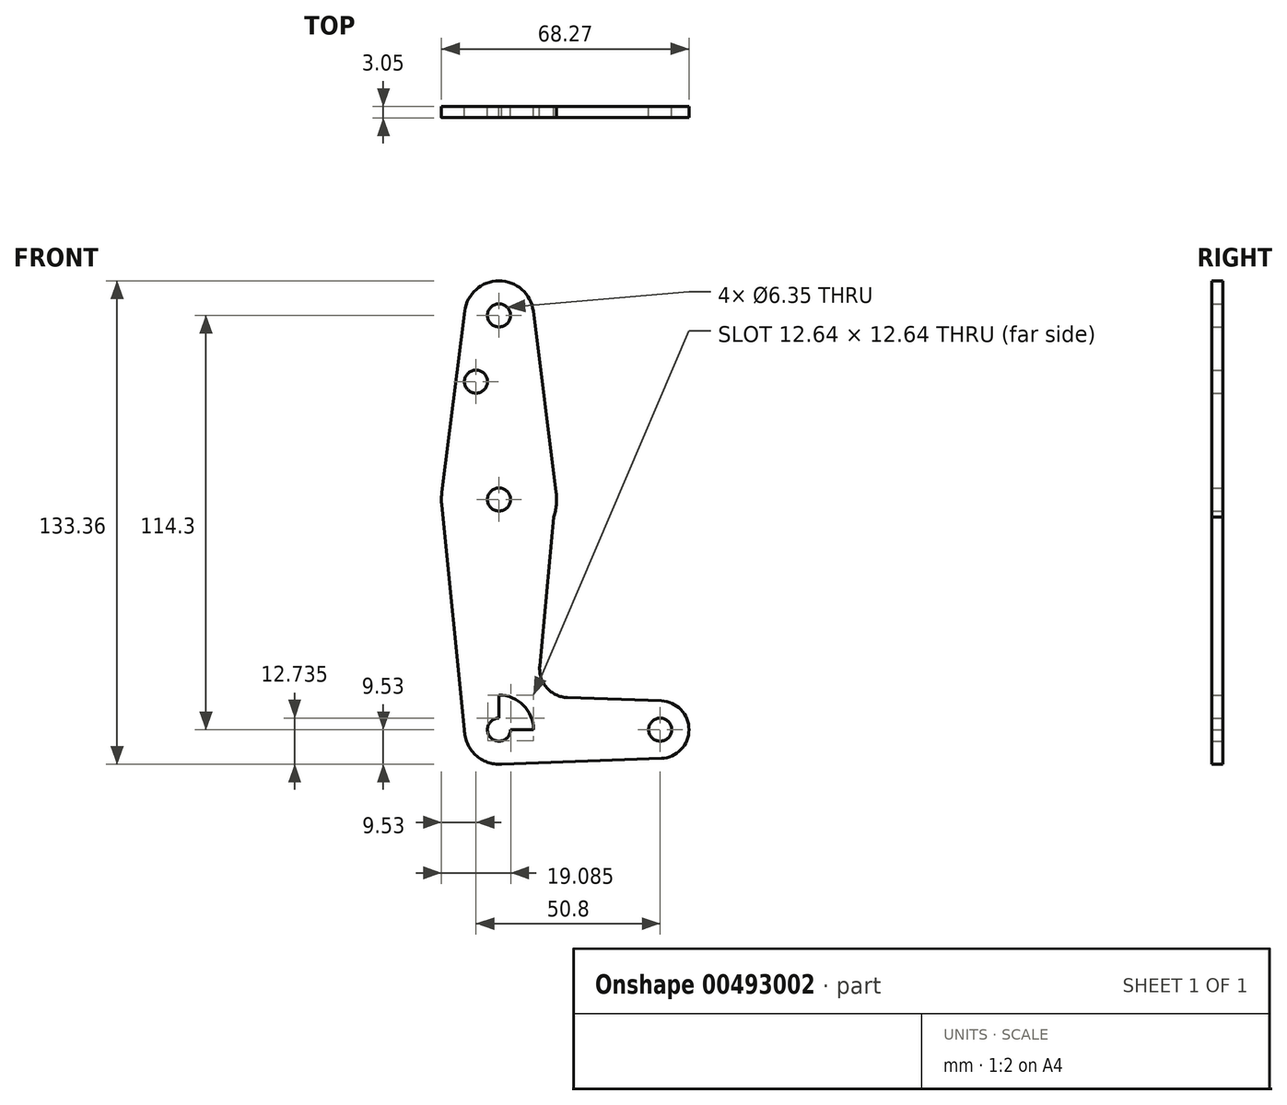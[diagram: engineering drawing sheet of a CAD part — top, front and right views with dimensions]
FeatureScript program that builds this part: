
annotation { "Feature Type Name" : "Feature", "Feature Type Description" : "" }
export const myFeature = defineFeature(function(context is Context, id is Id, definition is map)
    precondition{}
    {
        {
            var Q0;
            Q0=qCreatedBy(makeId("Front.planeOp"),FACE);
            var sketch = newSketch(context, id + "F0", { "sketchPlane" : qUnion([Q0])});
            skLineSegment(sketch, "E0", {"start": v(0, 0) * mm, "end": v(0, 114.3) * mm});
            skLineSegment(sketch, "E1", {"start": v(0, 114.3) * mm, "end": v(0, 0) * mm});
            skLineSegment(sketch, "E2", {"start": v(44.45, 0) * mm, "end": v(0, 0) * mm});
            skCircle(sketch, "E3", {"center": v(0, 114.3) * mm, "radius": 9.53 * mm});
            skCircle(sketch, "E4", {"center": v(0, 0) * mm, "radius": 9.53 * mm});
            skCircle(sketch, "E5", {"center": v(44.45, 0) * mm, "radius": 7.94 * mm});
            skCircle(sketch, "E6", {"center": v(0, 63.5) * mm, "radius": 15.88 * mm});
            skLineSegment(sketch, "E7", {"start": v(9.45, 115.5) * mm, "end": v(15.75, 65.48) * mm});
            skLineSegment(sketch, "E8", {"start": v(15.75, 65.48) * mm, "end": v(11.22, 17.55) * mm});
            skLineSegment(sketch, "E9", {"start": v(-9.45, 115.5) * mm, "end": v(-15.75, 65.48) * mm});
            skLineSegment(sketch, "E10", {"start": v(-15.75, 65.48) * mm, "end": v(-15.75, 61.52) * mm});
            skLineSegment(sketch, "E11", {"start": v(0, -9.53) * mm, "end": v(44.73, -7.93) * mm});
            skLineSegment(sketch, "E12", {"start": v(-9.53, 0) * mm, "end": v(-15.8, 61.9) * mm});
            skCircle(sketch, "E13", {"center": v(-6.35, 96.03) * mm, "radius": 3.18 * mm});
            skCircle(sketch, "E14", {"center": v(0, 63.5) * mm, "radius": 3.18 * mm});
            skCircle(sketch, "E15", {"center": v(0, 114.3) * mm, "radius": 3.18 * mm});
            skCircle(sketch, "E16", {"center": v(0, 0) * mm, "radius": 3.18 * mm});
            skCircle(sketch, "E17", {"center": v(44.45, 0) * mm, "radius": 3.18 * mm});
            skPoint(sketch, "E18.newPointA", {"position": v(0, 9.53) * mm});
            skLineSegment(sketch, "E19", {"start": v(18.86, 8.86) * mm, "end": v(44.73, 7.93) * mm});
            skArc(sketch, "E20.filletArc", {"start": v(11.22, 17.55) * mm, "mid": v(13.16, 11.56) * mm, "end": v(18.86, 8.86) * mm});
            skSolve(sketch);
        }
        {
            var Q0;
            Q0 = qSketchRegion(id + "F0", true);
            var Q1;
            {var subQ0=sQuery(id+"F0.wireOp",EDGE,"E4");var subQ1=sQuery(id+"F0.wireOp",EDGE,"E1");var subQ2=makeQuery(id+"F0.imprint","INTERSECT",VERTEX,{"derivedFrom":[subQ1,subQ0]});Q1=makeQuery(id+"F0.imprint","IMPRINT",FACE,{"disambiguationData":[TD([[makeQuery(id+"F0.imprint","IMPRINT",EDGE,{"disambiguationData":[TD([[subQ2,-1.0]])],"derivedFrom":subQ1}),1.0]])]});}
            extrude(context, id + "F1", {"entities" : qUnion([Q0, Q1]), "depth" : 3.05 * mm, "offsetDistance" : 25.4 * mm});
        }
    });
